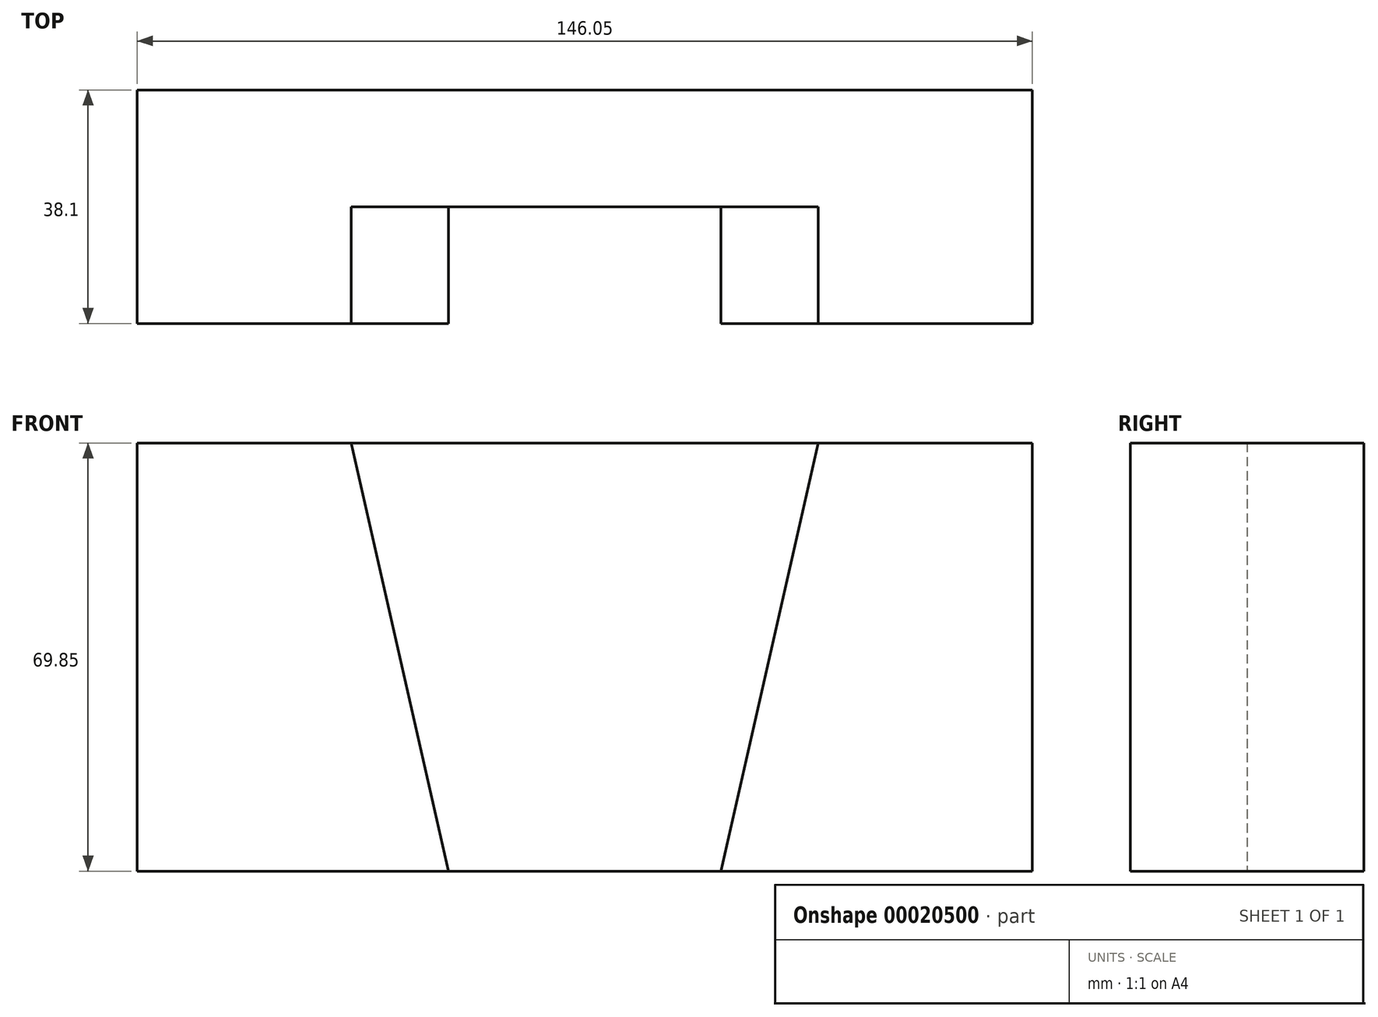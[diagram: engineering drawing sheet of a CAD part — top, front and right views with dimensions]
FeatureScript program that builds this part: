
annotation { "Feature Type Name" : "Feature", "Feature Type Description" : "" }
export const myFeature = defineFeature(function(context is Context, id is Id, definition is map)
    precondition{}
    {
        {
            var Q0;
            Q0=qCreatedBy(makeId("Front.planeOp"),FACE);
            var sketch = newSketch(context, id + "F0", { "sketchPlane" : qUnion([Q0])});
            skLineSegment(sketch, "E0", {"start": v(-37, 20.34) * mm, "end": v(-37, -49.5) * mm});
            skLineSegment(sketch, "E1", {"start": v(-37, 20.34) * mm, "end": v(36.02, 20.34) * mm});
            skLineSegment(sketch, "E2", {"start": v(36.02, 20.34) * mm, "end": v(36.02, -49.5) * mm});
            skLineSegment(sketch, "E3", {"start": v(36.02, -49.5) * mm, "end": v(-37, -49.5) * mm});
            skLineSegment(sketch, "E4", {"start": v(36.02, 20.34) * mm, "end": v(1.1, 20.34) * mm});
            skLineSegment(sketch, "E5", {"start": v(-14.78, -49.5) * mm, "end": v(36.02, -49.5) * mm});
            skLineSegment(sketch, "E6", {"start": v(1.1, 20.34) * mm, "end": v(-14.78, -49.5) * mm});
            skSolve(sketch);
        }
        {
            var Q0;
            Q0=makeQuery(id+"F0.imprint","IMPRINT",FACE,{"disambiguationData":[TD([[makeQuery(id+"F0.imprint","IMPRINT",EDGE,{"derivedFrom":sQuery(id+"F0.wireOp",EDGE,"E0")}),1.0]])]});
            extrude(context, id + "F1", {"entities" : qUnion([Q0]), "depth" : 19.05 * mm});
        }
        {
            var Q0;
            Q0=makeQuery(id+"F0.imprint","IMPRINT",FACE,{"disambiguationData":[TD([[makeQuery(id+"F0.imprint","IMPRINT",EDGE,{"derivedFrom":sQuery(id+"F0.wireOp",EDGE,"E2")}),-1.0]])]});
            extrude(context, id + "F2", {"entities" : qUnion([Q0]), "operationType" : NewBodyOperationType.ADD, "depth" : 38.1 * mm});
        }
        {
            var Q0;
            Q0=makeQuery(id+"F1.opExtrude","SWEPT_BODY",BODY,{"disambiguationData":[OSD([sQuery(id+"F0.wireOp",EDGE,"E0"),sQuery(id+"F0.wireOp",EDGE,"E1"),sQuery(id+"F0.wireOp",EDGE,"E3"),sQuery(id+"F0.wireOp",EDGE,"E6")])]});
            var Q1;
            Q1=makeQuery(id+"F1.opExtrude","SWEPT_FACE",FACE,{"disambiguationData":[OSD([sQuery(id+"F0.wireOp",EDGE,"E0")])]});
            mirror(context, id + "F3", {"operationType" : NewBodyOperationType.ADD, "entities" : qUnion([Q0]), "mirrorPlane" : qUnion([Q1])});
        }
    });
